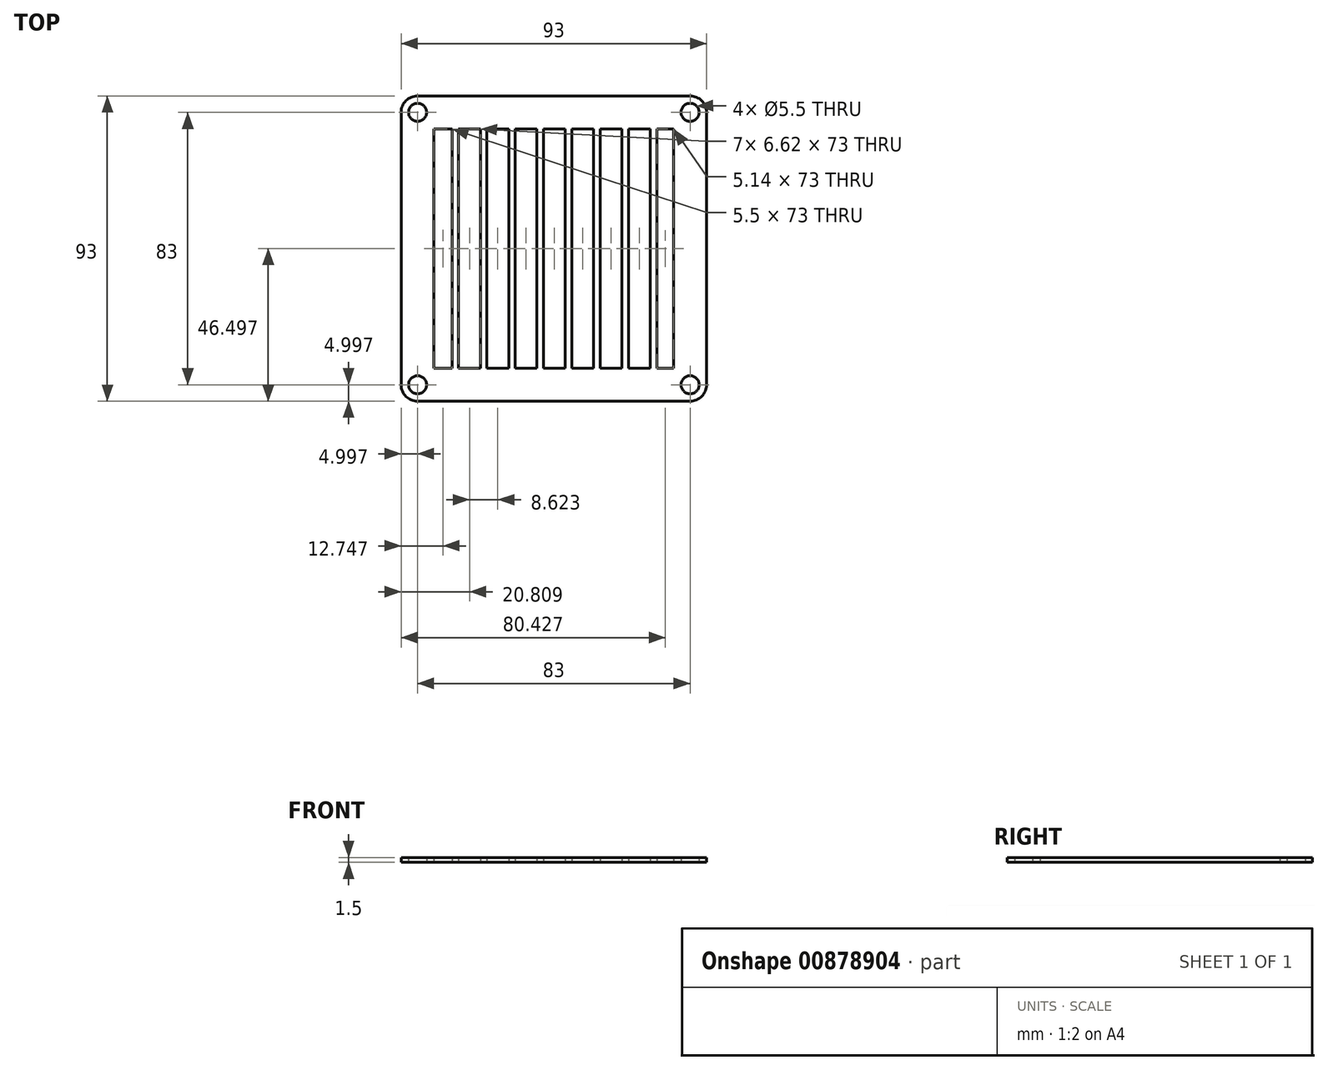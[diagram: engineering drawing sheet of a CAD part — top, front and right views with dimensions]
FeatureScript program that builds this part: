
annotation { "Feature Type Name" : "Feature", "Feature Type Description" : "" }
export const myFeature = defineFeature(function(context is Context, id is Id, definition is map)
    precondition{}
    {
        {
            var Q0;
            Q0=qCreatedBy(makeId("Top.planeOp"),FACE);
            var sketch = newSketch(context, id + "F0", { "sketchPlane" : qUnion([Q0])});
            skLineSegment(sketch, "E0.bottom", {"start": v(-36.72, 106.86) * mm, "end": v(46.28, 106.86) * mm, "construction": true});
            skLineSegment(sketch, "E0.top", {"start": v(-36.72, 23.86) * mm, "end": v(46.28, 23.86) * mm, "construction": true});
            skLineSegment(sketch, "E0.left", {"start": v(-36.72, 106.86) * mm, "end": v(-36.72, 23.86) * mm, "construction": true});
            skLineSegment(sketch, "E0.right", {"start": v(46.28, 106.86) * mm, "end": v(46.28, 23.86) * mm, "construction": true});
            skLineSegment(sketch, "E1.bottom", {"start": v(-41.72, 111.86) * mm, "end": v(51.28, 111.86) * mm});
            skLineSegment(sketch, "E1.top", {"start": v(-41.72, 18.86) * mm, "end": v(51.28, 18.86) * mm});
            skLineSegment(sketch, "E1.left", {"start": v(-41.72, 111.86) * mm, "end": v(-41.72, 18.86) * mm});
            skLineSegment(sketch, "E1.right", {"start": v(51.28, 111.86) * mm, "end": v(51.28, 18.86) * mm});
            skCircle(sketch, "E2", {"center": v(46.28, 106.86) * mm, "radius": 2.75 * mm});
            skCircle(sketch, "E3", {"center": v(-36.72, 106.86) * mm, "radius": 2.75 * mm});
            skCircle(sketch, "E4", {"center": v(-36.72, 23.86) * mm, "radius": 2.75 * mm});
            skCircle(sketch, "E5", {"center": v(46.28, 23.86) * mm, "radius": 2.75 * mm});
            skLineSegment(sketch, "E6.bottom", {"start": v(-31.72, 101.86) * mm, "end": v(41.28, 101.86) * mm});
            skLineSegment(sketch, "E6.top", {"start": v(-31.72, 28.86) * mm, "end": v(41.28, 28.86) * mm});
            skLineSegment(sketch, "E6.left", {"start": v(-31.72, 101.86) * mm, "end": v(-31.72, 28.86) * mm});
            skLineSegment(sketch, "E6.right", {"start": v(41.28, 101.86) * mm, "end": v(41.28, 28.86) * mm});
            skLineSegment(sketch, "E7.bottom", {"start": v(-26.22, 101.86) * mm, "end": v(-24.22, 101.86) * mm});
            skLineSegment(sketch, "E7.top", {"start": v(-26.22, 28.86) * mm, "end": v(-24.22, 28.86) * mm});
            skLineSegment(sketch, "E7.left", {"start": v(-26.22, 101.86) * mm, "end": v(-26.22, 28.86) * mm});
            skLineSegment(sketch, "E7.right", {"start": v(-24.22, 101.86) * mm, "end": v(-24.22, 28.86) * mm});
            skLineSegment(sketch, "E8.1.0.0", {"start": v(-17.6, 101.86) * mm, "end": v(-15.6, 101.86) * mm});
            skLineSegment(sketch, "E8.1.0.1", {"start": v(-15.6, 101.86) * mm, "end": v(-15.6, 28.86) * mm});
            skLineSegment(sketch, "E8.1.0.2", {"start": v(-17.6, 101.86) * mm, "end": v(-17.6, 28.86) * mm});
            skLineSegment(sketch, "E8.1.0.3", {"start": v(-17.6, 28.86) * mm, "end": v(-15.6, 28.86) * mm});
            skLineSegment(sketch, "E8.2.0.0", {"start": v(-8.98, 101.86) * mm, "end": v(-6.98, 101.86) * mm});
            skLineSegment(sketch, "E8.2.0.1", {"start": v(-6.98, 101.86) * mm, "end": v(-6.98, 28.86) * mm});
            skLineSegment(sketch, "E8.2.0.2", {"start": v(-8.98, 101.86) * mm, "end": v(-8.98, 28.86) * mm});
            skLineSegment(sketch, "E8.2.0.3", {"start": v(-8.98, 28.86) * mm, "end": v(-6.98, 28.86) * mm});
            skLineSegment(sketch, "E8.3.0.0", {"start": v(-0.35, 101.86) * mm, "end": v(1.65, 101.86) * mm});
            skLineSegment(sketch, "E8.3.0.1", {"start": v(1.65, 101.86) * mm, "end": v(1.65, 28.86) * mm});
            skLineSegment(sketch, "E8.3.0.2", {"start": v(-0.35, 101.86) * mm, "end": v(-0.35, 28.86) * mm});
            skLineSegment(sketch, "E8.3.0.3", {"start": v(-0.35, 28.86) * mm, "end": v(1.65, 28.86) * mm});
            skLineSegment(sketch, "E8.4.0.0", {"start": v(8.27, 101.86) * mm, "end": v(10.27, 101.86) * mm});
            skLineSegment(sketch, "E8.4.0.1", {"start": v(10.27, 101.86) * mm, "end": v(10.27, 28.86) * mm});
            skLineSegment(sketch, "E8.4.0.2", {"start": v(8.27, 101.86) * mm, "end": v(8.27, 28.86) * mm});
            skLineSegment(sketch, "E8.4.0.3", {"start": v(8.27, 28.86) * mm, "end": v(10.27, 28.86) * mm});
            skLineSegment(sketch, "E8.5.0.0", {"start": v(16.9, 101.86) * mm, "end": v(18.9, 101.86) * mm});
            skLineSegment(sketch, "E8.5.0.1", {"start": v(18.9, 101.86) * mm, "end": v(18.9, 28.86) * mm});
            skLineSegment(sketch, "E8.5.0.2", {"start": v(16.9, 101.86) * mm, "end": v(16.9, 28.86) * mm});
            skLineSegment(sketch, "E8.5.0.3", {"start": v(16.9, 28.86) * mm, "end": v(18.9, 28.86) * mm});
            skLineSegment(sketch, "E8.6.0.0", {"start": v(25.51, 101.86) * mm, "end": v(27.51, 101.86) * mm});
            skLineSegment(sketch, "E8.6.0.1", {"start": v(27.51, 101.86) * mm, "end": v(27.51, 28.86) * mm});
            skLineSegment(sketch, "E8.6.0.2", {"start": v(25.51, 101.86) * mm, "end": v(25.51, 28.86) * mm});
            skLineSegment(sketch, "E8.6.0.3", {"start": v(25.51, 28.86) * mm, "end": v(27.51, 28.86) * mm});
            skLineSegment(sketch, "E8.7.0.0", {"start": v(34.14, 101.86) * mm, "end": v(36.14, 101.86) * mm});
            skLineSegment(sketch, "E8.7.0.1", {"start": v(36.14, 101.86) * mm, "end": v(36.14, 28.86) * mm});
            skLineSegment(sketch, "E8.7.0.2", {"start": v(34.14, 101.86) * mm, "end": v(34.14, 28.86) * mm});
            skLineSegment(sketch, "E8.7.0.3", {"start": v(34.14, 28.86) * mm, "end": v(36.14, 28.86) * mm});
            skLineSegment(sketch, "E8.direction1", {"start": v(-26.42, 28.83) * mm, "end": v(-17.8, 28.83) * mm, "construction": true});
            skSolve(sketch);
        }
        {
            var Q0;
            Q0=makeQuery(id+"F0.imprint","IMPRINT",FACE,{"disambiguationData":[TD([[makeQuery(id+"F0.imprint","IMPRINT",EDGE,{"derivedFrom":sQuery(id+"F0.wireOp",EDGE,"E1.bottom")}),-1.0]])]});
            var Q1;
            {var subQ2=sQuery(id+"F0.wireOp",EDGE,"E7.left");Q1=makeQuery(id+"F0.imprint","IMPRINT",FACE,{"disambiguationData":[TD([[makeQuery(id+"F0.imprint","IMPRINT",EDGE,{"derivedFrom":subQ2}),1.0]])]});}
            var Q2;
            {var subQ0=sQuery(id+"F0.wireOp",EDGE,"E8.1.0.1");Q2=makeQuery(id+"F0.imprint","IMPRINT",FACE,{"disambiguationData":[TD([[makeQuery(id+"F0.imprint","IMPRINT",EDGE,{"derivedFrom":subQ0}),-1.0]])]});}
            var Q3;
            {var subQ0=sQuery(id+"F0.wireOp",EDGE,"E8.2.0.1");Q3=makeQuery(id+"F0.imprint","IMPRINT",FACE,{"disambiguationData":[TD([[makeQuery(id+"F0.imprint","IMPRINT",EDGE,{"derivedFrom":subQ0}),-1.0]])]});}
            var Q4;
            {var subQ0=sQuery(id+"F0.wireOp",EDGE,"E8.3.0.1");Q4=makeQuery(id+"F0.imprint","IMPRINT",FACE,{"disambiguationData":[TD([[makeQuery(id+"F0.imprint","IMPRINT",EDGE,{"derivedFrom":subQ0}),-1.0]])]});}
            var Q5;
            {var subQ0=sQuery(id+"F0.wireOp",EDGE,"E8.4.0.1");Q5=makeQuery(id+"F0.imprint","IMPRINT",FACE,{"disambiguationData":[TD([[makeQuery(id+"F0.imprint","IMPRINT",EDGE,{"derivedFrom":subQ0}),-1.0]])]});}
            var Q6;
            {var subQ0=sQuery(id+"F0.wireOp",EDGE,"E8.5.0.1");Q6=makeQuery(id+"F0.imprint","IMPRINT",FACE,{"disambiguationData":[TD([[makeQuery(id+"F0.imprint","IMPRINT",EDGE,{"derivedFrom":subQ0}),-1.0]])]});}
            var Q7;
            {var subQ0=sQuery(id+"F0.wireOp",EDGE,"E8.6.0.1");Q7=makeQuery(id+"F0.imprint","IMPRINT",FACE,{"disambiguationData":[TD([[makeQuery(id+"F0.imprint","IMPRINT",EDGE,{"derivedFrom":subQ0}),-1.0]])]});}
            var Q8;
            {var subQ0=sQuery(id+"F0.wireOp",EDGE,"E8.7.0.1");Q8=makeQuery(id+"F0.imprint","IMPRINT",FACE,{"disambiguationData":[TD([[makeQuery(id+"F0.imprint","IMPRINT",EDGE,{"derivedFrom":subQ0}),-1.0]])]});}
            extrude(context, id + "F1", {"entities" : qUnion([Q0, Q1, Q2, Q3, Q4, Q5, Q6, Q7, Q8]), "depth" : 1.5 * mm, "offsetDistance" : 25 * mm});
        }
        {
            var Q0;
            Q0=makeQuery(id+"F1.opExtrude","SWEPT_EDGE",EDGE,{"disambiguationData":[OSD([sQuery(id+"F0.wireOp",EDGE,"E1.bottom"),sQuery(id+"F0.wireOp",EDGE,"E1.left")])]});
            var Q1;
            Q1=makeQuery(id+"F1.opExtrude","SWEPT_EDGE",EDGE,{"disambiguationData":[OSD([sQuery(id+"F0.wireOp",EDGE,"E1.bottom"),sQuery(id+"F0.wireOp",EDGE,"E1.right")])]});
            var Q2;
            Q2=makeQuery(id+"F1.opExtrude","SWEPT_EDGE",EDGE,{"disambiguationData":[OSD([sQuery(id+"F0.wireOp",EDGE,"E1.top"),sQuery(id+"F0.wireOp",EDGE,"E1.right")])]});
            var Q3;
            Q3=makeQuery(id+"F1.opExtrude","SWEPT_EDGE",EDGE,{"disambiguationData":[OSD([sQuery(id+"F0.wireOp",EDGE,"E1.top"),sQuery(id+"F0.wireOp",EDGE,"E1.left")])]});
            fillet(context, id + "F2", {"entities" : qUnion([Q0, Q1, Q2, Q3]), "radius" : 5 * mm, "tangentPropagation" : true, "allowEdgeOverflow" : false});
        }
    });
